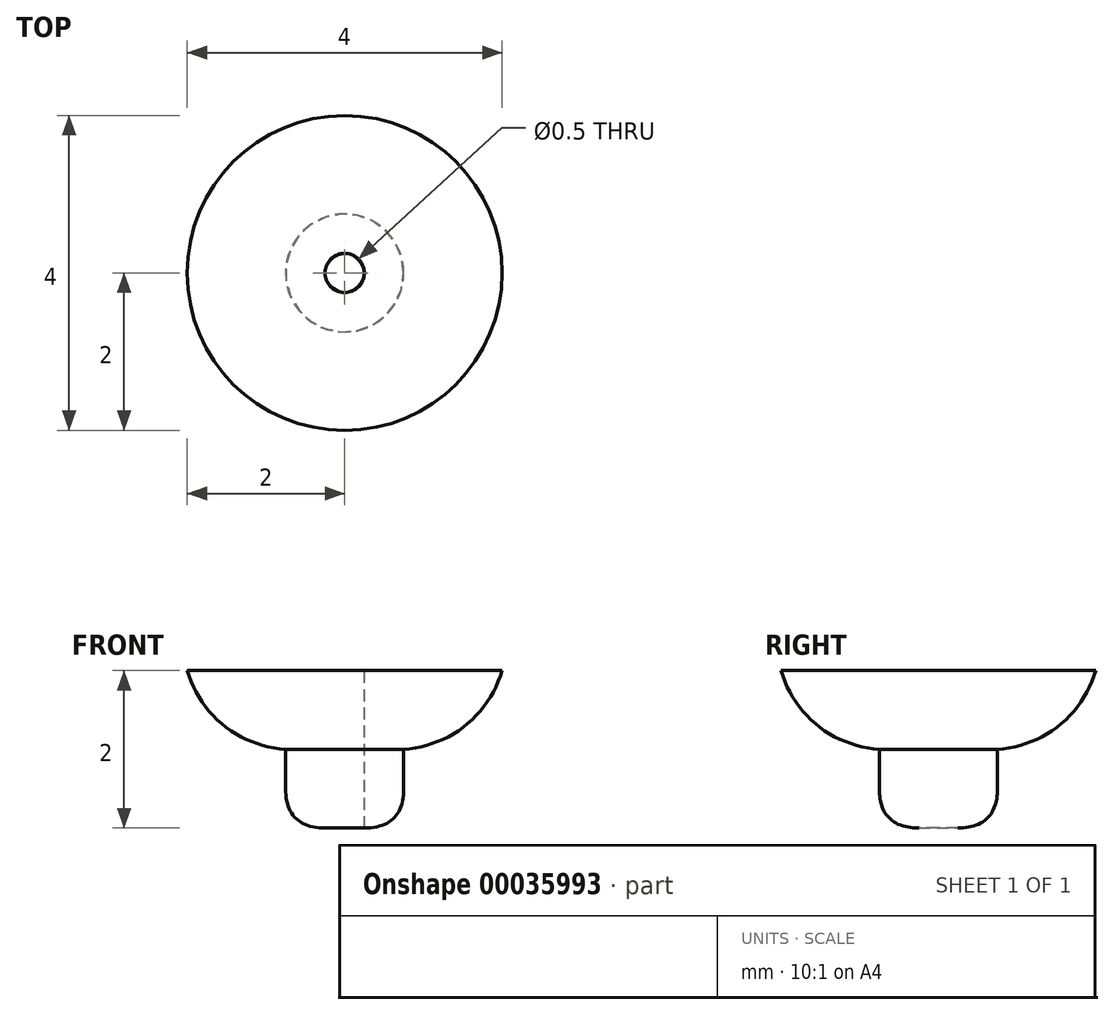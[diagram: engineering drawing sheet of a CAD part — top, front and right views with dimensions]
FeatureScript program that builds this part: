
annotation { "Feature Type Name" : "Feature", "Feature Type Description" : "" }
export const myFeature = defineFeature(function(context is Context, id is Id, definition is map)
    precondition{}
    {
        {
            var Q0;
            Q0=qCreatedBy(makeId("Front.planeOp"),FACE);
            var sketch = newSketch(context, id + "F0", { "sketchPlane" : qUnion([Q0])});
            skLineSegment(sketch, "E0", {"start": v(0, 0) * mm, "end": v(2, 0) * mm});
            skLineSegment(sketch, "E1", {"start": v(0, -2) * mm, "end": v(0.75, -2) * mm});
            skLineSegment(sketch, "E2", {"start": v(0, -2) * mm, "end": v(0, 0) * mm});
            skLineSegment(sketch, "E3", {"start": v(0.75, -2) * mm, "end": v(0.75, -1) * mm});
            skArc(sketch, "E4", {"start": v(0.75, -1) * mm, "mid": v(1.53, -0.7) * mm, "end": v(2, 0) * mm});
            skLineSegment(sketch, "E5", {"start": v(0, 1.64) * mm, "end": v(0, -4.9) * mm, "construction": true});
            skSolve(sketch);
        }
        {
            var Q0;
            Q0 = qSketchRegion(id + "F0", true);
            var Q1;
            Q1=sQuery(id+"F0.wireOp",EDGE,"E5");
            revolve(context, id + "F1", {"entities" : qUnion([Q0]), "axis" : qUnion([Q1]), "revolveType" : RevolveType.FULL});
        }
        {
            var Q0;
            Q0=makeQuery(id+"F1.opRevolve","SWEPT_FACE",FACE,{"disambiguationData":[OSD([sQuery(id+"F0.wireOp",EDGE,"E0")])]});
            var sketch = newSketch(context, id + "F2", { "sketchPlane" : qUnion([Q0])});
            skCircle(sketch, "E6", {"center": v(0, 0) * mm, "radius": 0.25 * mm});
            skSolve(sketch);
        }
        {
            var Q0;
            Q0 = qSketchRegion(id + "F2", true);
            extrude(context, id + "F3", {"entities" : qUnion([Q0]), "operationType" : NewBodyOperationType.REMOVE, "endBound" : BoundingType.THROUGH_ALL, "oppositeDirection" : true, "depth" : 25 * mm});
        }
        {
            var Q0;
            Q0=makeQuery(id+"F1.opRevolve","SWEPT_EDGE",EDGE,{"disambiguationData":[OSD([sQuery(id+"F0.wireOp",EDGE,"E1"),sQuery(id+"F0.wireOp",EDGE,"E3")])]});
            fillet(context, id + "F4", {"entities" : qUnion([Q0]), "radius" : .5 * mm, "tangentPropagation" : true, "rho" : 0.5, "crossSection" : FilletCrossSection.CONIC, "allowEdgeOverflow" : false});
        }
    });
